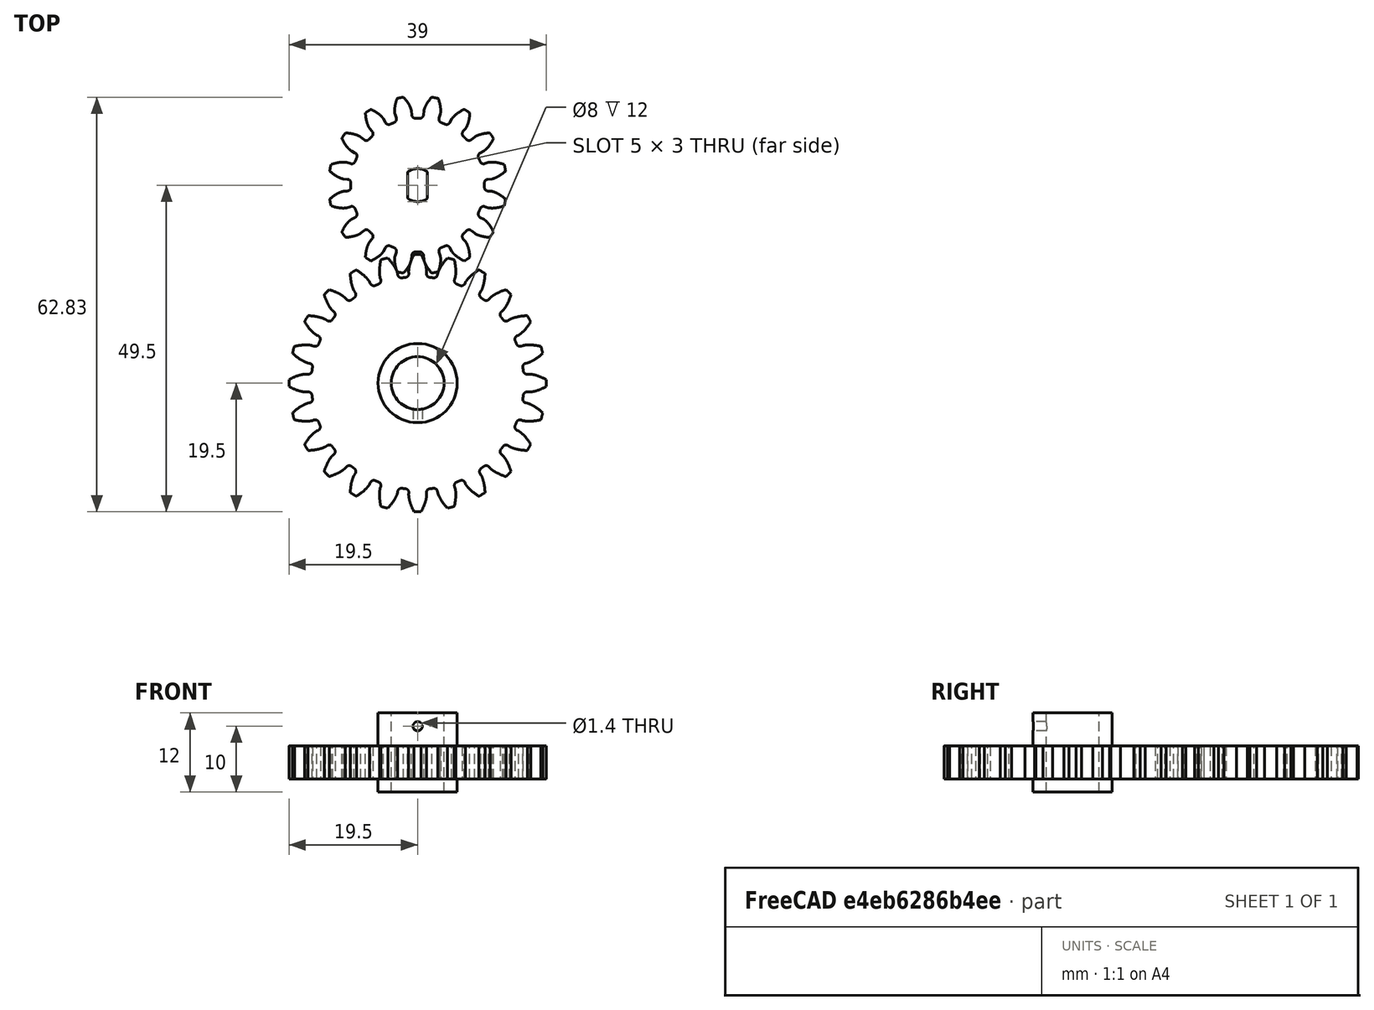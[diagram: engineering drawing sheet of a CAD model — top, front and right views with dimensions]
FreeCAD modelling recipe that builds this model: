
FCSTD DOCUMENT  (FreeCAD 0.16R6706 (Git))
Label: custom_gears
License: All rights reserved
LicenseURL: http://en.wikipedia.org/wiki/All_rights_reserved
objects: Part::Cylinder×10, Part::Cut×7, Part::Box×4, Part::MultiFuse×3, Part::Part2DObjectPython×2, PartDesign::Pad×2
note: 30 computed .brp shape members not serialized (recipe doc carries the construction recipe); baked Part::Feature solids carry a one-line shape summary decoded from their .brp

FEATURE [Part::Part2DObjectPython] InvoluteGear  # Draft 2D object (typed FeaturePython)
  ExternalGear = true
  HighPrecision = true
  Modules = 1.5
  NumberOfTeeth = 16
  Placement = pos=(0,0,0) rot=(0,0,1;0.19635rad)
  PressureAngle = 20
FEATURE [Part::Part2DObjectPython] InvoluteGear001  # Draft 2D object (typed FeaturePython)
  ExternalGear = true
  HighPrecision = true
  Modules = 1.5
  NumberOfTeeth = 24
  PressureAngle = 20
FEATURE [PartDesign::Pad] Pad
  Length = 5
  Length2 = 100
  Placement = pos=(0,0,0) rot=(0,0,1;0.19635rad)
  Sketch = -> InvoluteGear
  Type = 0
FEATURE [PartDesign::Pad] Pad001
  Length = 5
  Length2 = 100
  Sketch = -> InvoluteGear001
  Type = 0
FEATURE [Part::Cylinder] Cylinder
  Angle = 360
  Height = 15
  Placement = pos=(0,0,-2) rot=(0,0,1;0rad)
  Radius = 4
FEATURE [Part::Cylinder] Cylinder001
  Angle = 360
  Height = 19
  Radius = 14
FEATURE [Part::Cylinder] Cylinder002
  Angle = 360
  Height = 1.5
  Placement = pos=(-8,0,19) rot=(0,0,1;0rad)
  Radius = 4.5
FEATURE [Part::Cylinder] Cylinder003
  Angle = 360
  Height = 8.5
  Placement = pos=(-8,0,20.5) rot=(0,0,1;0rad)
  Radius = 2.5
FEATURE [Part::Cylinder] Cylinder004
  Angle = 360
  Height = 2
  Placement = pos=(0,-17.5,18) rot=(0,0,1;0rad)
  Radius = 2.1
FEATURE [Part::Cylinder] Cylinder005
  Angle = 360
  Height = 2
  Placement = pos=(0,17.5,18) rot=(0,0,1;0rad)
  Radius = 2.1
FEATURE [Part::Cylinder] Cylinder006
  Angle = 360
  Height = 0.75
  Placement = pos=(0,-17.5,18) rot=(0,0,1;0rad)
  Radius = 3.5
FEATURE [Part::Cylinder] Cylinder007
  Angle = 360
  Height = 0.75
  Placement = pos=(0,17.5,18) rot=(0,0,1;0rad)
  Radius = 3.5
FEATURE [Part::Box] Box  label="Cube"
  Height = 0.75
  Length = 7
  Placement = pos=(-3.5,-17.5,18) rot=(0,0,1;0rad)
  Width = 35
FEATURE [Part::MultiFuse] Fusion
  Placement = pos=(0,0,0.25) rot=(0,0,1;0rad)
  Shapes = -> [Cylinder006,Cylinder007,Box]
FEATURE [Part::Cut] Cut001
  Base = -> Fusion
  Tool = -> Cylinder004
FEATURE [Part::Cut] Cut002
  Base = -> Cut001
  Tool = -> Cylinder005
FEATURE [Part::Box] Box001  label="Cube001"
  Height = 16.5
  Length = 17
  Placement = pos=(0,-7.3,2.5) rot=(0,0,1;0rad)
  Width = 14.6
FEATURE [Part::Box] Box002  label="Cube002"
  Height = 6
  Length = 1
  Placement = pos=(-6.5,-2.5,23) rot=(0,0,1;0rad)
  Width = 5
FEATURE [Part::Box] Box003  label="Cube003"
  Height = 6
  Length = 1
  Placement = pos=(-10.5,-2.5,23) rot=(0,0,1;0rad)
  Width = 5
FEATURE [Part::Cut] Cut003
  Base = -> Cylinder003
  Tool = -> Box002
FEATURE [Part::Cut] Cut004
  Base = -> Cut003
  Tool = -> Box003
FEATURE [Part::MultiFuse] Fusion001  label="motor"
  Placement = pos=(8,0,-23.5) rot=(0,0,1;0rad)
  Shapes = -> [Cut004,Box001,Cut002,Cylinder002,Cylinder001]
FEATURE [Part::Cut] Cut005  label="small gear"
  Base = -> Pad
  Placement = pos=(0,30,0) rot=(0,0,1;0rad)
  Tool = -> Fusion001
FEATURE [Part::Cylinder] Cylinder008
  Angle = 360
  Height = 12
  Placement = pos=(0,0,-2) rot=(0,0,1;0rad)
  Radius = 6
FEATURE [Part::MultiFuse] Fusion002
  Shapes = -> [Cylinder008,Pad001]
FEATURE [Part::Cut] Cut
  Base = -> Fusion002
  Tool = -> Cylinder
FEATURE [Part::Cylinder] Cylinder009
  Angle = 360
  Height = 10
  Placement = pos=(0,0,8) rot=(1,0,0;1.5708rad)
  Radius = 0.7
FEATURE [Part::Cut] Cut006  label="big gear"
  Base = -> Cut
  Tool = -> Cylinder009
